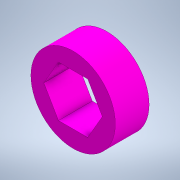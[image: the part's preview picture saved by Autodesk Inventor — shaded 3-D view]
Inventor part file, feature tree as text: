
AUTODESK INVENTOR PART (.ipt)
format: ipt  version: 2021.2 (Build 252289000, 289)  size: 107,008 bytes
history: native  units: in
note: dims shown in document units (in); Inventor stores cm internally (conversion verified against a paired STEP export)
features: extrude x1, sketch x1
ambient origin geometry x8: Origin, YZ Plane, XZ Plane, XY Plane, X Axis, Y Axis, Z Axis, Center Point
bodies: Solid1 (feature_tree)
feature tree (2):
  extrude  "Extrusion1"  Depth=0.25in
  sketch  "Sketch1"  dims[d0=0.375in d2=0.625in d3=0.096in d4=0.25in d5=0.0in]
